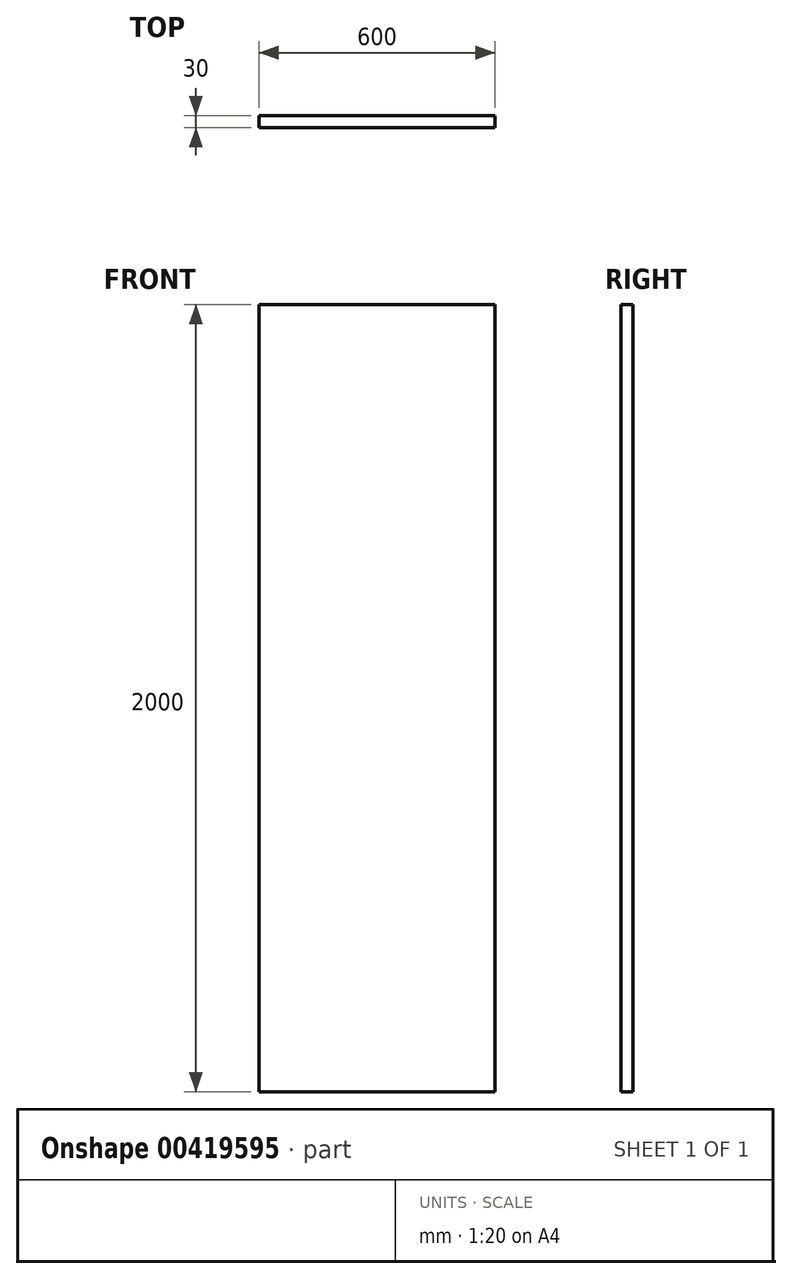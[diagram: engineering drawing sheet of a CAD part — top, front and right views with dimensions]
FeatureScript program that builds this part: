
annotation { "Feature Type Name" : "Feature", "Feature Type Description" : "" }
export const myFeature = defineFeature(function(context is Context, id is Id, definition is map)
    precondition{}
    {
        {
            var Q0;
            Q0=qCreatedBy(makeId("Top.planeOp"),FACE);
            var sketch = newSketch(context, id + "F0", { "sketchPlane" : qUnion([Q0])});
            skLineSegment(sketch, "E0.bottom", {"start": v(-454.83, 14.35) * mm, "end": v(145.17, 14.35) * mm});
            skLineSegment(sketch, "E0.top", {"start": v(-454.83, -15.65) * mm, "end": v(145.17, -15.65) * mm});
            skLineSegment(sketch, "E0.left", {"start": v(-454.83, 14.35) * mm, "end": v(-454.83, -15.65) * mm});
            skLineSegment(sketch, "E0.right", {"start": v(145.17, 14.35) * mm, "end": v(145.17, -15.65) * mm});
            skSolve(sketch);
        }
        {
            var Q0;
            Q0=makeQuery(id+"F0.imprint","IMPRINT",FACE,{"disambiguationData":[TD([[makeQuery(id+"F0.imprint","IMPRINT",EDGE,{"derivedFrom":sQuery(id+"F0.wireOp",EDGE,"E0.bottom")}),-1.0]])]});
            extrude(context, id + "F1", {"entities" : qUnion([Q0]), "depth" : 2000 * mm});
        }
    });
